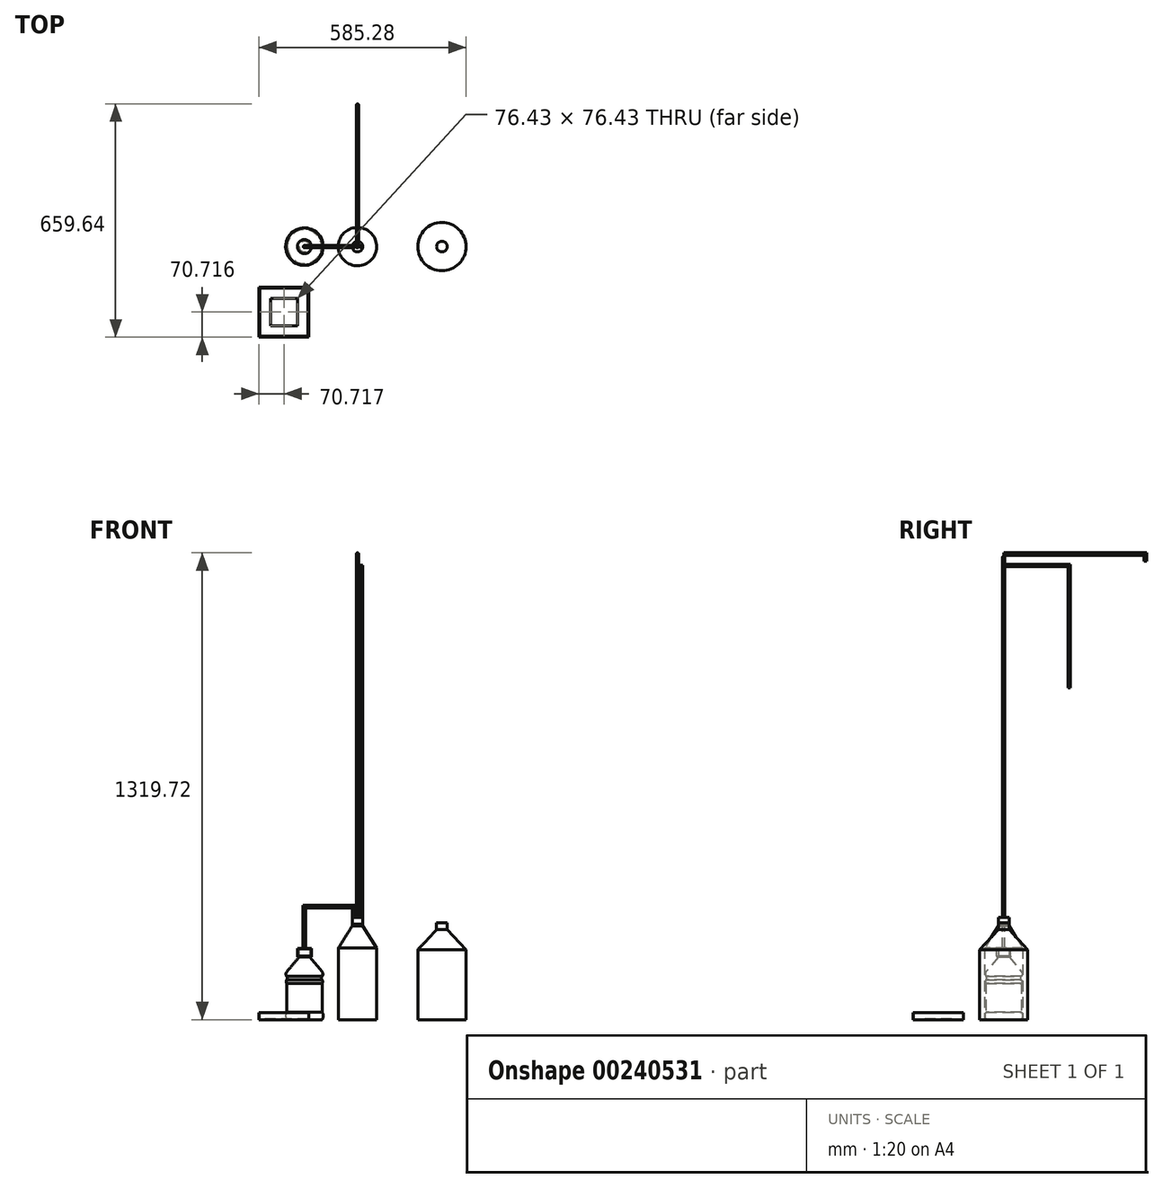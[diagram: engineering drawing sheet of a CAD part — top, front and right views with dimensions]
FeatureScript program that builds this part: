
annotation { "Feature Type Name" : "Feature", "Feature Type Description" : "" }
export const myFeature = defineFeature(function(context is Context, id is Id, definition is map)
    precondition{}
    {
        {
            var Q0;
            Q0=qCreatedBy(makeId("Front.planeOp"),FACE);
            var sketch = newSketch(context, id + "F0", { "sketchPlane" : qUnion([Q0])});
            skLineSegment(sketch, "E0", {"start": v(0, 0) * mm, "end": v(0, 200) * mm});
            skLineSegment(sketch, "E1", {"start": v(0, 200) * mm, "end": v(15, 200) * mm});
            skLineSegment(sketch, "E2", {"start": v(15, 200) * mm, "end": v(15, 180) * mm});
            skLineSegment(sketch, "E3", {"start": v(0, 0) * mm, "end": v(50, 0) * mm});
            skLineSegment(sketch, "E4", {"start": v(15, 180) * mm, "end": v(20, 180) * mm});
            skLineSegment(sketch, "E5", {"start": v(20, 180) * mm, "end": v(20, 177) * mm});
            skLineSegment(sketch, "E6", {"start": v(20, 177) * mm, "end": v(15, 177) * mm});
            skLineSegment(sketch, "E7", {"start": v(15, 177) * mm, "end": v(50, 135.1) * mm});
            skLineSegment(sketch, "E8", {"start": v(50, 102.55) * mm, "end": v(50, 21.63) * mm});
            skArc(sketch, "E9", {"start": v(50, 122.28) * mm, "mid": v(52.33, 128.7) * mm, "end": v(50, 135.1) * mm});
            skArc(sketch, "E10", {"start": v(50, 122.28) * mm, "mid": v(48.22, 117.61) * mm, "end": v(50, 112.94) * mm});
            skArc(sketch, "E11", {"start": v(50, 102.55) * mm, "mid": v(51.46, 107.75) * mm, "end": v(50, 112.94) * mm});
            skArc(sketch, "E12", {"start": v(50, 0) * mm, "mid": v(53.18, 10.82) * mm, "end": v(50, 21.63) * mm});
            skLineSegment(sketch, "E13", {"start": v(0, 0) * mm, "end": v(150, 0) * mm});
            skLineSegment(sketch, "E14", {"start": v(150, 0) * mm, "end": v(150, 270) * mm});
            skLineSegment(sketch, "E15", {"start": v(150, 270) * mm, "end": v(165, 270) * mm});
            skLineSegment(sketch, "E16", {"start": v(165, 270) * mm, "end": v(165, 265) * mm});
            skLineSegment(sketch, "E17", {"start": v(165, 265) * mm, "end": v(204.08, 202.08) * mm});
            skLineSegment(sketch, "E18", {"start": v(204.08, 202.08) * mm, "end": v(204.08, 0) * mm});
            skLineSegment(sketch, "E19", {"start": v(204.08, 0) * mm, "end": v(150, 0) * mm});
            skLineSegment(sketch, "E20", {"start": v(204.08, 0) * mm, "end": v(388.58, 0) * mm});
            skLineSegment(sketch, "E21", {"start": v(388.58, 0) * mm, "end": v(388.58, 274.31) * mm});
            skLineSegment(sketch, "E22", {"start": v(388.58, 274.31) * mm, "end": v(403.58, 274.31) * mm});
            skLineSegment(sketch, "E23", {"start": v(403.58, 274.31) * mm, "end": v(403.58, 254.31) * mm});
            skLineSegment(sketch, "E24", {"start": v(403.58, 254.31) * mm, "end": v(456.75, 197.4) * mm});
            skLineSegment(sketch, "E25", {"start": v(456.75, 197.4) * mm, "end": v(456.75, 0) * mm});
            skLineSegment(sketch, "E26", {"start": v(456.75, 0) * mm, "end": v(388.58, 0) * mm});
            skSolve(sketch);
        }
        {
            var Q0;
            Q0=makeQuery(id+"F0.imprint","IMPRINT",FACE,{"disambiguationData":[TD([[makeQuery(id+"F0.imprint","IMPRINT",EDGE,{"derivedFrom":sQuery(id+"F0.wireOp",EDGE,"E0")}),-1.0]])]});
            var Q1;
            Q1=sQuery(id+"F0.wireOp",EDGE,"E0");
            revolve(context, id + "F1", {"entities" : qUnion([Q0]), "axis" : qUnion([Q1]), "revolveType" : RevolveType.FULL});
        }
        {
            var Q0;
            Q0=makeQuery(id+"F1.opRevolve","SWEPT_FACE",FACE,{"disambiguationData":[OSD([sQuery(id+"F0.wireOp",EDGE,"E1")])]});
            var sketch = newSketch(context, id + "F2", { "sketchPlane" : qUnion([Q0])});
            skCircle(sketch, "E27.0", {"center": v(0, 0) * mm, "radius": 20 * mm});
            skSolve(sketch);
        }
        {
            var Q0;
            Q0=makeQuery(id+"F2.imprint","IMPRINT",FACE,{"disambiguationData":[TD([[makeQuery(id+"F2.imprint","IMPRINT",EDGE,{"derivedFrom":sQuery(id+"F2.wireOp",EDGE,"E27.0")}),1.0]])]});
            var Q1;
            Q1=makeQuery(id+"F2.imprint","IMPRINT",FACE,{"disambiguationData":[TD([[makeQuery(id+"F2.imprint","IMPRINT",EDGE,{"derivedFrom":makeQuery(id+"F1.opRevolve","SWEPT_EDGE",EDGE,{"disambiguationData":[OSD([sQuery(id+"F0.wireOp",EDGE,"E1"),sQuery(id+"F0.wireOp",EDGE,"E2")])]})}),-1.0]])]});
            extrude(context, id + "F3", {"entities" : qUnion([Q0, Q1]), "depth" : 1.9 * mm});
        }
        {
            var Q0;
            Q0=makeQuery(id+"F3.opExtrude","CAP_FACE",FACE,{"disambiguationData":[OSD([sQuery(id+"F2.wireOp",EDGE,"E27.0")])],"isStart":true});
            extrude(context, id + "F4", {"entities" : qUnion([Q0]), "depth" : 19.7 * mm});
        }
        {
            var Q0;
            Q0=makeQuery(id+"F0.imprint","IMPRINT",FACE,{"disambiguationData":[TD([[makeQuery(id+"F0.imprint","IMPRINT",EDGE,{"derivedFrom":sQuery(id+"F0.wireOp",EDGE,"E14")}),-1.0]])]});
            var Q1;
            Q1=sQuery(id+"F0.wireOp",EDGE,"E14");
            revolve(context, id + "F5", {"entities" : qUnion([Q0]), "axis" : qUnion([Q1]), "revolveType" : RevolveType.FULL});
        }
        {
            var Q0;
            Q0=makeQuery(id+"F5.opRevolve","SWEPT_FACE",FACE,{"disambiguationData":[OSD([sQuery(id+"F0.wireOp",EDGE,"E15")])]});
            extrude(context, id + "F6", {"entities" : qUnion([Q0]), "depth" : 19 * mm});
        }
        {
            var Q0;
            Q0=makeQuery(id+"F3.opExtrude","CAP_FACE",FACE,{"disambiguationData":[OSD([sQuery(id+"F2.wireOp",EDGE,"E27.0")])],"isStart":false});
            var sketch = newSketch(context, id + "F7", { "sketchPlane" : qUnion([Q0])});
            skCircle(sketch, "E28", {"center": v(0, 0) * mm, "radius": 3.5 * mm});
            skSolve(sketch);
        }
        {
            var Q0;
            Q0=qCreatedBy(makeId("Front.planeOp"),FACE);
            var sketch = newSketch(context, id + "F8", { "sketchPlane" : qUnion([Q0])});
            skLineSegment(sketch, "E29", {"start": v(0, 201.9) * mm, "end": v(0, 319.36) * mm});
            skLineSegment(sketch, "E30", {"start": v(0, 319.36) * mm, "end": v(139.4, 319.36) * mm});
            skLineSegment(sketch, "E31", {"start": v(139.4, 278.72) * mm, "end": v(139.4, 319.36) * mm});
            skLineSegment(sketch, "E32", {"start": v(139.4, 278.72) * mm, "end": v(160.8, 278.72) * mm});
            skLineSegment(sketch, "E33", {"start": v(150.1, 278.72) * mm, "end": v(150.1, 1284.38) * mm});
            skLineSegment(sketch, "E34", {"start": v(160.8, 278.72) * mm, "end": v(160.8, 1284.38) * mm});
            skLineSegment(sketch, "E35", {"start": v(150.1, 278.72) * mm, "end": v(150.1, 0) * mm});
            skCircle(sketch, "E36", {"center": v(150.1, 1284.38) * mm, "radius": 3.5 * mm});
            skLineSegment(sketch, "E37", {"start": v(150.1, 1284.38) * mm, "end": v(150.1, 1319.23) * mm});
            skCircle(sketch, "E38", {"center": v(150.1, 1316.22) * mm, "radius": 3.5 * mm});
            skSolve(sketch);
        }
        {
            var Q0;
            Q0=makeQuery(id+"F7.imprint","IMPRINT",FACE,{"disambiguationData":[TD([[makeQuery(id+"F7.imprint","IMPRINT",EDGE,{"derivedFrom":sQuery(id+"F7.wireOp",EDGE,"E28")}),1.0]])]});
            var Q1;
            Q1=sQuery(id+"F8.wireOp",EDGE,"E29");
            var Q2;
            Q2=sQuery(id+"F8.wireOp",EDGE,"E30");
            var Q3;
            Q3=sQuery(id+"F8.wireOp",EDGE,"E31");
            var Q4;
            Q4=sQuery(id+"F8.wireOp",EDGE,"E34");
            var Q5;
            Q5=sQuery(id+"F8.wireOp",EDGE,"E32");
            sweep(context, id + "F9", {"operationType" : NewBodyOperationType.ADD, "profiles" : qUnion([Q0]), "path" : qUnion([Q1, Q2, Q3, Q4, Q5])});
        }
        {
            var Q0;
            Q0=makeQuery(id+"F6.opExtrude","CAP_FACE",FACE,{"disambiguationData":[OSD([sQuery(id+"F0.wireOp",EDGE,"E15")])],"isStart":false});
            var sketch = newSketch(context, id + "F10", { "sketchPlane" : qUnion([Q0])});
            skCircle(sketch, "E39", {"center": v(150, 0) * mm, "radius": 3.5 * mm});
            skSolve(sketch);
        }
        {
            var Q0;
            Q0=makeQuery(id+"F10.imprint","IMPRINT",FACE,{"disambiguationData":[TD([[makeQuery(id+"F10.imprint","IMPRINT",EDGE,{"derivedFrom":sQuery(id+"F10.wireOp",EDGE,"E39")}),1.0]])]});
            var Q1;
            Q1=sQuery(id+"F8.wireOp",EDGE,"E33");
            sweep(context, id + "F11", {"operationType" : NewBodyOperationType.ADD, "profiles" : qUnion([Q0]), "path" : qUnion([Q1])});
        }
        {
            var Q0;
            Q0=makeQuery(id+"F0.imprint","IMPRINT",FACE,{"disambiguationData":[TD([[makeQuery(id+"F0.imprint","IMPRINT",EDGE,{"derivedFrom":sQuery(id+"F0.wireOp",EDGE,"E21")}),-1.0]])]});
            var Q1;
            Q1=sQuery(id+"F0.wireOp",EDGE,"E21");
            revolve(context, id + "F12", {"entities" : qUnion([Q0]), "axis" : qUnion([Q1]), "revolveType" : RevolveType.FULL});
        }
        {
            var Q0;
            Q0=qCreatedBy(makeId("Top.planeOp"),FACE);
            var sketch = newSketch(context, id + "F13", { "sketchPlane" : qUnion([Q0])});
            skLineSegment(sketch, "E40.bottom", {"start": v(12.9, -255.93) * mm, "end": v(-128.53, -255.93) * mm});
            skLineSegment(sketch, "E40.top", {"start": v(12.9, -114.5) * mm, "end": v(-128.53, -114.5) * mm});
            skLineSegment(sketch, "E40.left", {"start": v(12.9, -255.93) * mm, "end": v(12.9, -114.5) * mm});
            skLineSegment(sketch, "E40.right", {"start": v(-128.53, -255.93) * mm, "end": v(-128.53, -114.5) * mm});
            skPoint(sketch, "E40.middle", {"position": v(-57.81, -185.21) * mm});
            skSolve(sketch);
        }
        {
            var Q0;
            Q0=makeQuery(id+"F13.imprint","IMPRINT",FACE,{"disambiguationData":[TD([[makeQuery(id+"F13.imprint","IMPRINT",EDGE,{"derivedFrom":sQuery(id+"F13.wireOp",EDGE,"E40.bottom")}),-1.0]])]});
            extrude(context, id + "F14", {"entities" : qUnion([Q0]), "depth" : 20 * mm});
        }
        {
            var Q0;
            Q0=makeQuery(id+"F14.opExtrude","CAP_FACE",FACE,{"disambiguationData":[OSD([sQuery(id+"F13.wireOp",EDGE,"E40.bottom"),sQuery(id+"F13.wireOp",EDGE,"E40.top"),sQuery(id+"F13.wireOp",EDGE,"E40.left"),sQuery(id+"F13.wireOp",EDGE,"E40.right")])],"isStart":false});
            shell(context, id + "F15", {"entities" : qUnion([Q0]), "thickness" : 2.5 * mm});
        }
        {
            var Q0;
            Q0=makeQuery(id+"F15.opShell","OFFSET_FACE",FACE,{"disambiguationData":[OSD([sQuery(id+"F13.wireOp",EDGE,"E40.bottom"),sQuery(id+"F13.wireOp",EDGE,"E40.top"),sQuery(id+"F13.wireOp",EDGE,"E40.left"),sQuery(id+"F13.wireOp",EDGE,"E40.right")])]});
            var sketch = newSketch(context, id + "F16", { "sketchPlane" : qUnion([Q0])});
            skLineSegment(sketch, "E41.0", {"start": v(-19.6, -223.43) * mm, "end": v(-19.6, -147) * mm});
            skLineSegment(sketch, "E41.1", {"start": v(-96.03, -223.43) * mm, "end": v(-19.6, -223.43) * mm});
            skLineSegment(sketch, "E41.2", {"start": v(-96.03, -147) * mm, "end": v(-96.03, -223.43) * mm});
            skLineSegment(sketch, "E41.3", {"start": v(-19.6, -147) * mm, "end": v(-96.03, -147) * mm});
            skSolve(sketch);
        }
        {
            var Q0;
            Q0=makeQuery(id+"F16.imprint","IMPRINT",FACE,{"disambiguationData":[TD([[makeQuery(id+"F16.imprint","IMPRINT",EDGE,{"derivedFrom":sQuery(id+"F16.wireOp",EDGE,"E41.0")}),1.0]])]});
            extrude(context, id + "F17", {"entities" : qUnion([Q0]), "operationType" : NewBodyOperationType.REMOVE, "oppositeDirection" : true, "depth" : 25 * mm});
        }
        {
            var Q0;
            Q0=qCreatedBy(makeId("Right.planeOp"),FACE);
            cPlane(context, id + "F18", {"entities" : qUnion([Q0]), "cplaneType" : CPlaneType.OFFSET, "offset" : 150.1 * mm, "width" : 150 * mm, "height" : 150 * mm});
        }
        {
            var Q0;
            Q0=qCreatedBy(id+"F18.planeOp",FACE);
            var sketch = newSketch(context, id + "F19", { "sketchPlane" : qUnion([Q0])});
            skLineSegment(sketch, "E42", {"start": v(0, 1284.24) * mm, "end": v(185, 1284.24) * mm});
            skLineSegment(sketch, "E43", {"start": v(185, 1284.24) * mm, "end": v(185, 1177.98) * mm});
            skLineSegment(sketch, "E44", {"start": v(0, 1316.01) * mm, "end": v(400, 1316.01) * mm});
            skLineSegment(sketch, "E45", {"start": v(400, 1316.01) * mm, "end": v(400, 1296.01) * mm});
            skSolve(sketch);
        }
        {
            var Q0;
            Q0=makeQuery(id+"F8.imprint","IMPRINT",FACE,{"disambiguationData":[TD([[makeQuery(id+"F8.imprint","IMPRINT",EDGE,{"derivedFrom":sQuery(id+"F8.wireOp",EDGE,"E36")}),1.0]])]});
            var Q1;
            Q1=sQuery(id+"F8.wireOp",EDGE,"E36");
            var Q2;
            Q2=sQuery(id+"F19.wireOp",EDGE,"E42");
            var Q3;
            Q3=sQuery(id+"F19.wireOp",EDGE,"E43");
            sweep(context, id + "F20", {"profiles" : qUnion([Q0]), "surfaceProfiles" : qUnion([Q1]), "path" : qUnion([Q2, Q3])});
        }
        {
            var Q0;
            Q0=makeQuery(id+"F20.opSweep","CAP_FACE",FACE,{"disambiguationData":[OSD([sQuery(id+"F8.wireOp",EDGE,"E36"),sQuery(id+"F19.wireOp",VERTEX,"efLYprI8-USB9-8g2L-eX0T-70GJ8cbX2GFe.end")])],"isStart":false});
            extrude(context, id + "F21", {"entities" : qUnion([Q0]), "operationType" : NewBodyOperationType.ADD, "depth" : 90 * mm});
        }
        {
            var Q0;
            Q0=makeQuery(id+"F21.opExtrude","CAP_FACE",FACE,{"disambiguationData":[OSD([sQuery(id+"F8.wireOp",EDGE,"E36"),sQuery(id+"F19.wireOp",VERTEX,"E43.end")])],"isStart":false});
            extrude(context, id + "F22", {"entities" : qUnion([Q0]), "operationType" : NewBodyOperationType.ADD, "depth" : 150 * mm});
        }
        {
            var Q0;
            Q0=makeQuery(id+"F11.opSweep","CAP_FACE",FACE,{"disambiguationData":[OSD([sQuery(id+"F8.wireOp",VERTEX,"E33.end"),sQuery(id+"F10.wireOp",EDGE,"E39")])],"isStart":false});
            extrude(context, id + "F23", {"entities" : qUnion([Q0]), "operationType" : NewBodyOperationType.ADD, "depth" : 25 * mm});
        }
        {
            var Q0;
            Q0=makeQuery(id+"F8.imprint","IMPRINT",FACE,{"disambiguationData":[TD([[makeQuery(id+"F8.imprint","IMPRINT",EDGE,{"derivedFrom":sQuery(id+"F8.wireOp",EDGE,"E38")}),1.0]])]});
            var Q1;
            Q1=sQuery(id+"F19.wireOp",EDGE,"E44");
            var Q2;
            Q2=sQuery(id+"F19.wireOp",EDGE,"E45");
            sweep(context, id + "F24", {"profiles" : qUnion([Q0]), "path" : qUnion([Q1, Q2])});
        }
    });
